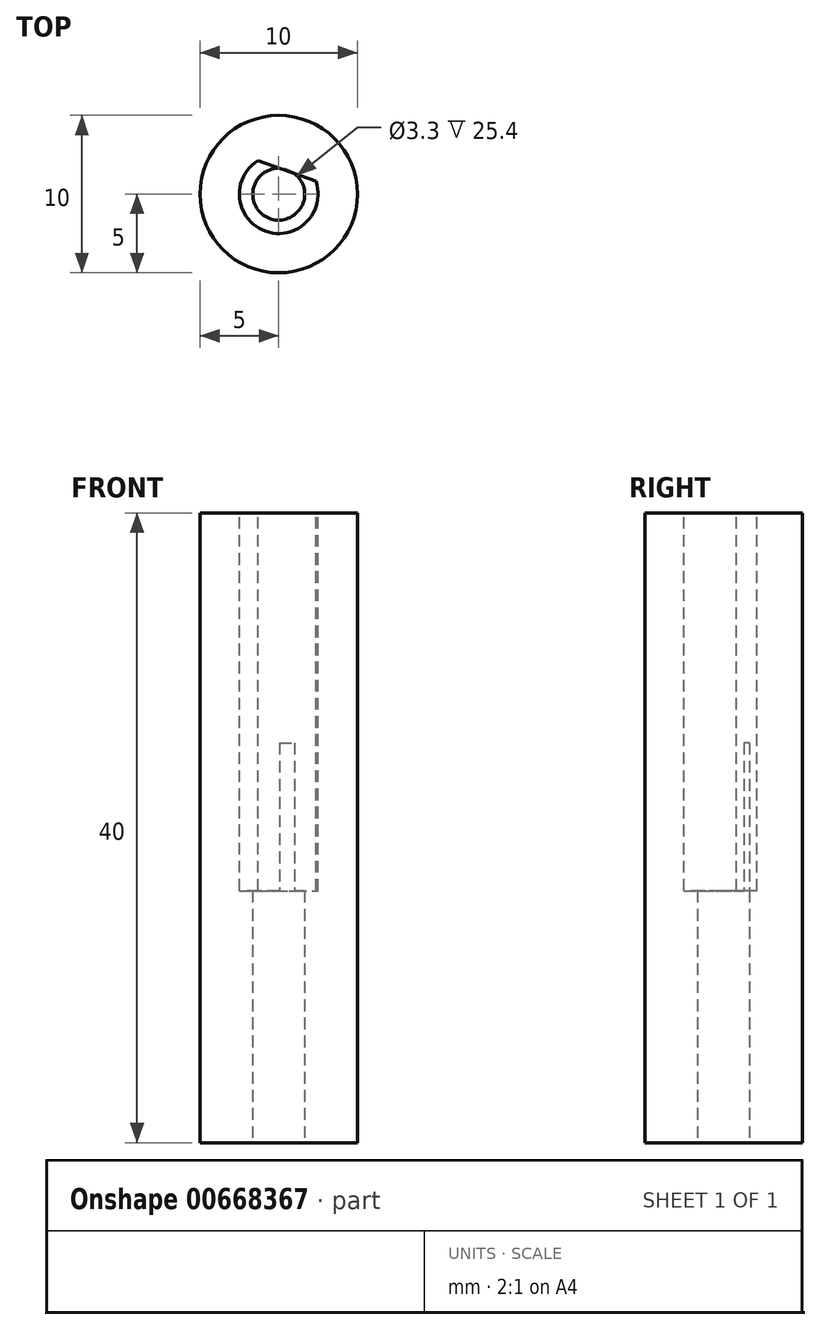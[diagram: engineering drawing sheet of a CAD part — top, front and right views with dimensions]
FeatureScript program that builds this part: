
annotation { "Feature Type Name" : "Feature", "Feature Type Description" : "" }
export const myFeature = defineFeature(function(context is Context, id is Id, definition is map)
    precondition{}
    {
        {
            var Q0;
            Q0=qCreatedBy(makeId("Top.planeOp"),FACE);
            var sketch = newSketch(context, id + "F0", { "sketchPlane" : qUnion([Q0])});
            skCircle(sketch, "E0", {"center": v(0, 0) * mm, "radius": 5 * mm});
            skSolve(sketch);
        }
        {
            var Q0;
            Q0 = qSketchRegion(id + "F0", true);
            extrude(context, id + "F1", {"entities" : qUnion([Q0]), "depth" : 40 * mm, "offsetDistance" : 25.4 * mm});
        }
        {
            var Q0;
            Q0=makeQuery(id+"F1.opExtrude","CAP_FACE",FACE,{"disambiguationData":[OSD([sQuery(id+"F0.wireOp",EDGE,"E0")])],"isStart":false});
            var sketch = newSketch(context, id + "F2", { "sketchPlane" : qUnion([Q0])});
            skCircle(sketch, "E1", {"center": v(0, 0) * mm, "radius": 2.5 * mm});
            skLineSegment(sketch, "E2", {"start": v(-1.3, 2.13) * mm, "end": v(2.36, 0.83) * mm});
            skSolve(sketch);
        }
        {
            var Q0;
            {var subQ0=sQuery(id+"F2.wireOp",EDGE,"E2");Q0=makeQuery(id+"F2.imprint","IMPRINT",FACE,{"disambiguationData":[TD([[makeQuery(id+"F2.imprint","IMPRINT",EDGE,{"derivedFrom":subQ0}),-1.0]])]});}
            extrude(context, id + "F3", {"entities" : qUnion([Q0]), "operationType" : NewBodyOperationType.REMOVE, "oppositeDirection" : true, "depth" : 24 * mm, "offsetDistance" : 25.4 * mm});
        }
        {
            var Q0;
            Q0=makeQuery(id+"F1.opExtrude","CAP_FACE",FACE,{"disambiguationData":[OSD([sQuery(id+"F0.wireOp",EDGE,"E0")])],"isStart":true});
            var sketch = newSketch(context, id + "F4", { "sketchPlane" : qUnion([Q0])});
            skCircle(sketch, "E3", {"center": v(0, 0) * mm, "radius": 1.65 * mm});
            skSolve(sketch);
        }
        {
            var Q0;
            Q0=makeQuery(id+"F4.imprint","IMPRINT",FACE,{"disambiguationData":[TD([[makeQuery(id+"F4.imprint","IMPRINT",EDGE,{"derivedFrom":sQuery(id+"F4.wireOp",EDGE,"E3")}),1.0]])]});
            extrude(context, id + "F5", {"entities" : qUnion([Q0]), "operationType" : NewBodyOperationType.REMOVE, "oppositeDirection" : true, "depth" : 25.4 * mm, "offsetDistance" : 25.4 * mm});
        }
    });
